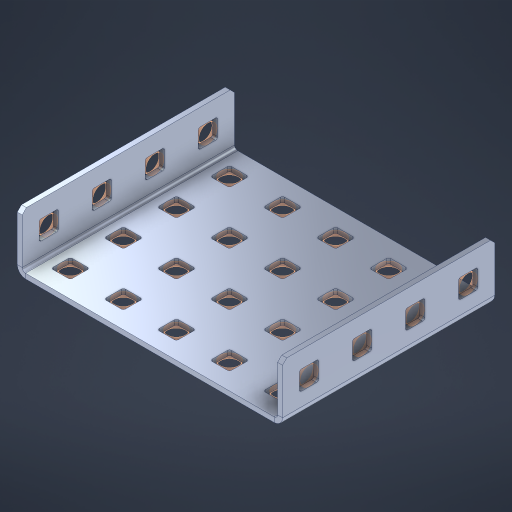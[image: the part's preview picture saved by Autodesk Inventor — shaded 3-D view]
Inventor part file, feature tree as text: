
AUTODESK INVENTOR PART (.ipt)
format: ipt  version: 2023 (Build 270158000, 158)  size: 628,224 bytes
history: native  units: in
note: dims shown in document units (in); Inventor stores cm internally (conversion verified against a paired STEP export)
features: other x33, extrude x27, sheet_metal_op x10, sketch x8, mirror x1, pattern_linear x1, chamfer x1
ambient origin geometry x8: Origin, YZ Plane, XZ Plane, XY Plane, X Axis, Y Axis, Z Axis, Center Point
bodies: Solid1 (feature_tree), Body (feature_tree)
feature tree (81):
  other  "Flange Pattern Plane"
  sheet_metal_op  "Flange Pattern"
  sheet_metal_op  "Body Pattern"
  other  "Arc Length"
  mirror  "Notch Mirror"
  pattern_linear  "Notch Pattern"  Spacing1=0.1875in  [1 undecoded]
  chamfer  "End Chamfer"
  extrude  "Half Cut"  Depth=0.0469in
  sketch  "Sketch1"  dims[d0=2.5in]
  other  "Plate1"
  sketch  "Sketch2"  dims[d1=2.0in]
  other  "Plate2"
  sheet_metal_op  "Bend1"
  sheet_metal_op  "Corner1"
  sketch  "Sketch3"  dims[d2=0.0469in]
  other  "Flange Pattern Sketch"
  sketch  "Sketch7"  dims[d3=0.0469in]
  other  "Srf1"
  other  "Srf2"
  sketch  "Sketch8"  dims[d4=0.0234in]
  sketch  "Sketch9"  dims[d5=0.0938in]
  other  "Srf91"
  sheet_metal_op  "Body Pattern Sketch"
  other  "Srf92"
  sketch  "Sketch13"  dims[d6=0.0469in]
  sketch  "Sketch14"  dims[d7=0.5in d8=90.0deg d9=0.0312in d10=0.1875in d11=0.0469in d12=0.0469in d16=0.182in d17=0.02in d18=0.0469in d19=0.0in d20=0.25in d21=0.25in d46=0.172in d47=1.0in d48=0.0in d49=0.182in d50=0.02in d51=0.25in d52=0.25in d53=0.0469in d54=0.0in d55=0.172in d56=1.0in d57=0.0in d60=1.5748in d62=0.5in d63=1.9685in d65=0.5in d85=0.1227in d86=0.1659in d88=0.04in d89=0.0469in d90=0.0in d91=0.04in d92=0.0491in d95=2.5in d96=0.04in d97=0.25in d98=45.0deg d101=0.0in d102=2.497in d131=2.5in d132=1.5748in d134=0.5in d139=0.5in]
  other  "Srf856"
  other  "Srf1310"
  other  "Srf1311"
  other  "Srf1312"
  other  "Srf1376"
  other  "Srf1377"
  other  "Srf1728"
  other  "Srf1755"
  other  "Srf1878"
  other  "Srf1879"
  other  "Srf1942"
  other  "Srf1943"
  other  "Srf1944"
  other  "Srf1945"
  other  "Srf1946"
  other  "Srf1947"
  other  "Srf1948"
  other  "Srf1949"
  other  "Srf1950"
  other  "Srf1951"
  other  "Srf1952"
  other  "Srf1953"
  other  "Srf1954"
  other  "Srf1955"
  sheet_metal_op  "Flange Stamp"
  sheet_metal_op  "Flange Circle"
  sheet_metal_op  "Body Stamp"
  sheet_metal_op  "Body Circle"
  sheet_metal_op  "Notch"
  extrude  "ExtrusionSrf2"  Depth=0.0469in
  extrude  "ExtrusionSrf92"  Depth=0.182in
  extrude  "ExtrusionSrf856"  Depth=0.02in
  extrude  "ExtrusionSrf1310"  Depth=0.0469in
  extrude  "ExtrusionSrf1311"  TaperAngle=0.0deg  [1 undecoded]
  extrude  "ExtrusionSrf1312"  Depth=0.25in
  extrude  "ExtrusionSrf1376"  Depth=0.25in
  extrude  "ExtrusionSrf1377"  Depth=0.5in
  extrude  "ExtrusionSrf1728"  Depth=1.0in TaperAngle=0.0deg
  extrude  "ExtrusionSrf1755"  Depth=0.182in
  extrude  "ExtrusionSrf1878"  Depth=0.02in
  extrude  "ExtrusionSrf1879"  Depth=0.25in
  extrude  "ExtrusionSrf1942"  Depth=0.25in
  extrude  "ExtrusionSrf1943"  Depth=0.0469in
  extrude  "ExtrusionSrf1944"  TaperAngle=0.0deg  [1 undecoded]
  extrude  "ExtrusionSrf1945"  Depth=0.5in
  extrude  "ExtrusionSrf1946"  Depth=1.0in TaperAngle=0.0deg
  extrude  "ExtrusionSrf1947"  Depth=0.5in
  extrude  "ExtrusionSrf1948"  Depth=0.5in
  extrude  "ExtrusionSrf1949"  Depth=0.5in
  extrude  "ExtrusionSrf1950"  Depth=0.5in
  extrude  "ExtrusionSrf1951"  Depth=0.5in
  extrude  "ExtrusionSrf1952"  Depth=0.0469in
  extrude  "ExtrusionSrf1953"  TaperAngle=0.0deg  [1 undecoded]
  extrude  "ExtrusionSrf1954"  Depth=0.5in
  extrude  "ExtrusionSrf1955"  Depth=0.5in
note: 4 required parameter values undecoded (feature->parameter linkage not recoverable at this tier; creation-order binding heuristic only, values carry confidence <= 0.55)
